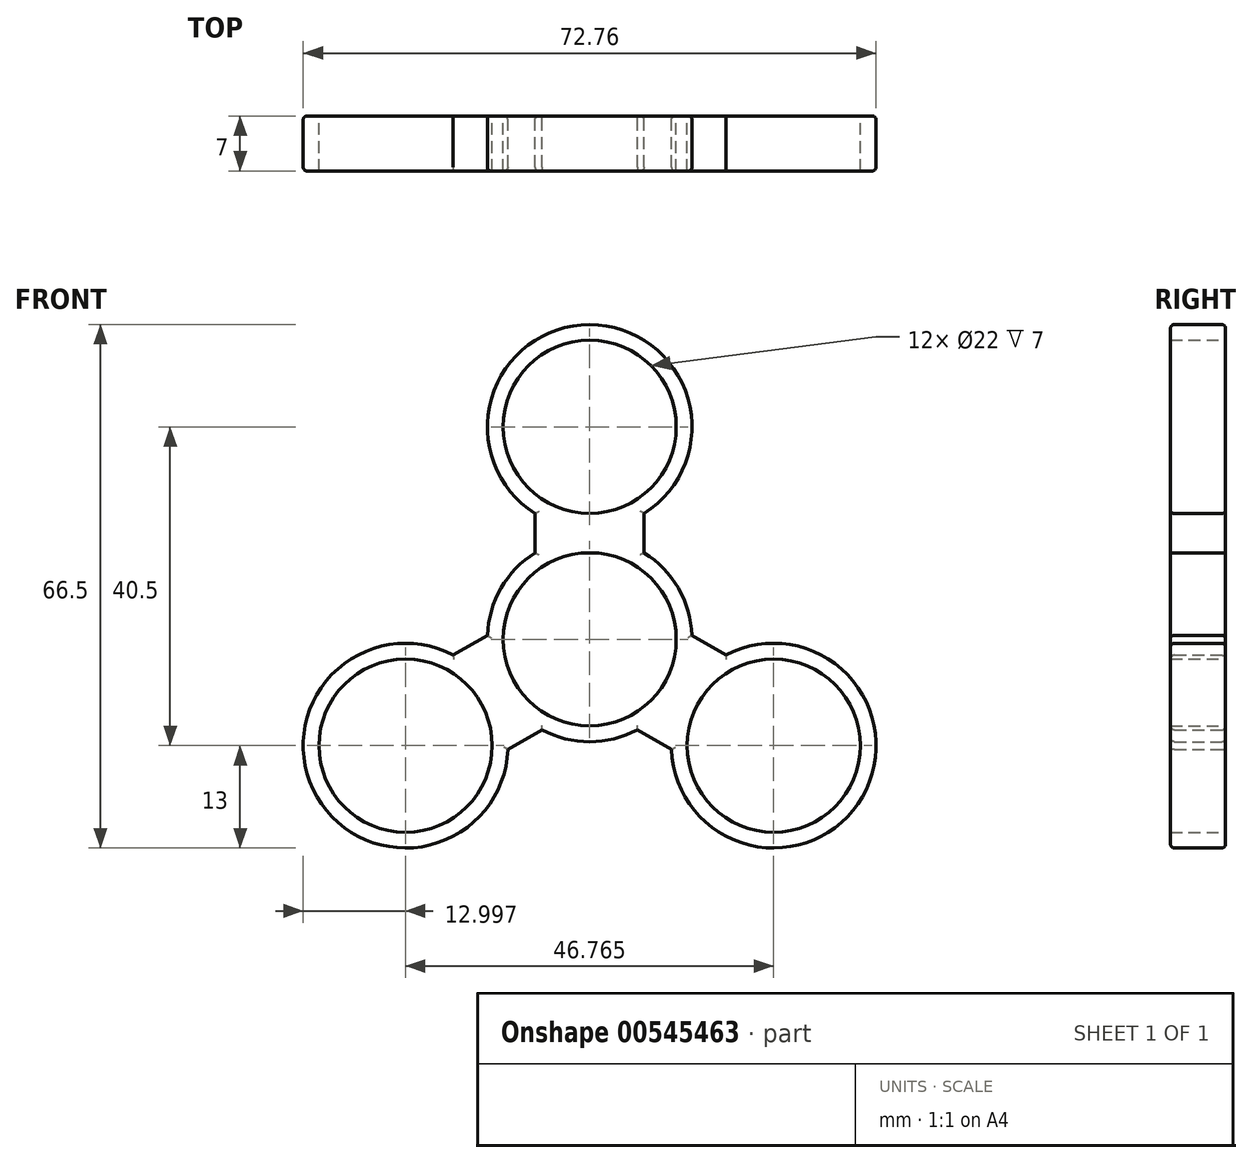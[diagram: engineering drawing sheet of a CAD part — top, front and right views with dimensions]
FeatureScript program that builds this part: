
annotation { "Feature Type Name" : "Feature", "Feature Type Description" : "" }
export const myFeature = defineFeature(function(context is Context, id is Id, definition is map)
    precondition{}
    {
        {
            var Q0;
            Q0=qCreatedBy(makeId("Front.planeOp"),FACE);
            var sketch = newSketch(context, id + "F0", { "sketchPlane" : qUnion([Q0])});
            skCircle(sketch, "E0", {"center": v(0, 0) * mm, "radius": 11 * mm});
            skCircle(sketch, "E1", {"center": v(0, 0) * mm, "radius": 13 * mm});
            skPoint(sketch, "E2", {"position": v(0, 27) * mm});
            skCircle(sketch, "E3", {"center": v(0, 27) * mm, "radius": 11 * mm});
            skCircle(sketch, "E4", {"center": v(0, 27) * mm, "radius": 13 * mm});
            skLineSegment(sketch, "E5", {"start": v(0, 0) * mm, "end": v(23.38, -13.5) * mm});
            skCircle(sketch, "E6", {"center": v(23.38, -13.5) * mm, "radius": 11 * mm});
            skCircle(sketch, "E7", {"center": v(23.38, -13.5) * mm, "radius": 13 * mm});
            skLineSegment(sketch, "E8", {"start": v(0, 0) * mm, "end": v(-23.38, -13.5) * mm});
            skCircle(sketch, "E9", {"center": v(-23.38, -13.5) * mm, "radius": 11 * mm});
            skCircle(sketch, "E10", {"center": v(-23.38, -13.5) * mm, "radius": 13 * mm});
            skLineSegment(sketch, "E11.left", {"start": v(6.93, 16) * mm, "end": v(6.93, 11) * mm});
            skLineSegment(sketch, "E11.right", {"start": v(-6.93, 16) * mm, "end": v(-6.93, 11) * mm});
            skPoint(sketch, "E11.middle", {"position": v(0, 13.5) * mm});
            skLineSegment(sketch, "E12", {"start": v(13, 0.5) * mm, "end": v(17.32, -2) * mm});
            skLineSegment(sketch, "E13", {"start": v(6.06, -11.5) * mm, "end": v(10.4, -14) * mm});
            skLineSegment(sketch, "E14", {"start": v(-17.32, -2) * mm, "end": v(-13, 0.5) * mm});
            skLineSegment(sketch, "E15", {"start": v(-10.4, -14) * mm, "end": v(-6.06, -11.5) * mm});
            skSolve(sketch);
        }
        {
            var Q0;
            Q0 = qSketchRegion(id + "F0", true);
            extrude(context, id + "F1", {"entities" : qUnion([Q0]), "endBound" : BoundingType.SYMMETRIC, "depth" : 7 * mm, "offsetDistance" : 25.4 * mm});
        }
        {
            var Q0;
            Q0=makeQuery(id+"F1.opExtrude","CAP_EDGE",EDGE,{"disambiguationData":[OSD([sQuery(id+"F0.wireOp",EDGE,"E4")])],"isStart":false});
            var Q1;
            Q1=makeQuery(id+"F1.opExtrude","CAP_EDGE",EDGE,{"disambiguationData":[OSD([sQuery(id+"F0.wireOp",EDGE,"E4")])],"isStart":true});
            var Q2;
            Q2=makeQuery(id+"F1.opExtrude","CAP_EDGE",EDGE,{"disambiguationData":[OSD([sQuery(id+"F0.wireOp",EDGE,"E11.left")])],"isStart":false});
            var Q3;
            Q3=makeQuery(id+"F1.opExtrude","CAP_EDGE",EDGE,{"disambiguationData":[OSD([sQuery(id+"F0.wireOp",EDGE,"E11.left")])],"isStart":true});
            var Q4;
            Q4=makeQuery(id+"F1.opExtrude","CAP_EDGE",EDGE,{"disambiguationData":[OSD([sQuery(id+"F0.wireOp",EDGE,"E11.right")])],"isStart":false});
            var Q5;
            Q5=makeQuery(id+"F1.opExtrude","CAP_EDGE",EDGE,{"disambiguationData":[OSD([sQuery(id+"F0.wireOp",EDGE,"E11.right")])],"isStart":true});
            var Q6;
            {var subQ0=sQuery(id+"F0.wireOp",EDGE,"E1");Q6=makeQuery(id+"F1.opExtrude","CAP_EDGE",EDGE,{"disambiguationData":[OSD([subQ0]),TDD([makeQuery(id+"F0.imprint","IMPRINT",EDGE,{"disambiguationData":[TD([[makeQuery(id+"F0.imprint","INTERSECT",VERTEX,{"derivedFrom":[subQ0,sQuery(id+"F0.wireOp",EDGE,"E11.right")]}),-1.0]])],"derivedFrom":subQ0})])],"isStart":true});}
            var Q7;
            {var subQ0=sQuery(id+"F0.wireOp",EDGE,"E1");Q7=makeQuery(id+"F1.opExtrude","CAP_EDGE",EDGE,{"disambiguationData":[OSD([subQ0]),TDD([makeQuery(id+"F0.imprint","IMPRINT",EDGE,{"disambiguationData":[TD([[makeQuery(id+"F0.imprint","INTERSECT",VERTEX,{"derivedFrom":[subQ0,sQuery(id+"F0.wireOp",EDGE,"E11.right")]}),-1.0]])],"derivedFrom":subQ0})])],"isStart":false});}
            var Q8;
            Q8=makeQuery(id+"F1.opExtrude","CAP_EDGE",EDGE,{"disambiguationData":[OSD([sQuery(id+"F0.wireOp",EDGE,"E14")])],"isStart":true});
            var Q9;
            Q9=makeQuery(id+"F1.opExtrude","CAP_EDGE",EDGE,{"disambiguationData":[OSD([sQuery(id+"F0.wireOp",EDGE,"E15")])],"isStart":true});
            var Q10;
            Q10=makeQuery(id+"F1.opExtrude","CAP_EDGE",EDGE,{"disambiguationData":[OSD([sQuery(id+"F0.wireOp",EDGE,"E10")])],"isStart":true});
            var Q11;
            Q11=makeQuery(id+"F1.opExtrude","CAP_EDGE",EDGE,{"disambiguationData":[OSD([sQuery(id+"F0.wireOp",EDGE,"E10")])],"isStart":false});
            var Q12;
            Q12=makeQuery(id+"F1.opExtrude","CAP_EDGE",EDGE,{"disambiguationData":[OSD([sQuery(id+"F0.wireOp",EDGE,"E14")])],"isStart":false});
            var Q13;
            Q13=makeQuery(id+"F1.opExtrude","CAP_EDGE",EDGE,{"disambiguationData":[OSD([sQuery(id+"F0.wireOp",EDGE,"E15")])],"isStart":false});
            var Q14;
            {var subQ0=sQuery(id+"F0.wireOp",EDGE,"E1");Q14=makeQuery(id+"F1.opExtrude","CAP_EDGE",EDGE,{"disambiguationData":[OSD([subQ0]),TDD([makeQuery(id+"F0.imprint","IMPRINT",EDGE,{"disambiguationData":[TD([[makeQuery(id+"F0.imprint","INTERSECT",VERTEX,{"derivedFrom":[subQ0,sQuery(id+"F0.wireOp",EDGE,"E13")]}),1.0]])],"derivedFrom":subQ0})])],"isStart":false});}
            var Q15;
            {var subQ0=sQuery(id+"F0.wireOp",EDGE,"E1");Q15=makeQuery(id+"F1.opExtrude","CAP_EDGE",EDGE,{"disambiguationData":[OSD([subQ0]),TDD([makeQuery(id+"F0.imprint","IMPRINT",EDGE,{"disambiguationData":[TD([[makeQuery(id+"F0.imprint","INTERSECT",VERTEX,{"derivedFrom":[subQ0,sQuery(id+"F0.wireOp",EDGE,"E13")]}),1.0]])],"derivedFrom":subQ0})])],"isStart":true});}
            var Q16;
            Q16=makeQuery(id+"F1.opExtrude","CAP_EDGE",EDGE,{"disambiguationData":[OSD([sQuery(id+"F0.wireOp",EDGE,"E13")])],"isStart":false});
            var Q17;
            Q17=makeQuery(id+"F1.opExtrude","CAP_EDGE",EDGE,{"disambiguationData":[OSD([sQuery(id+"F0.wireOp",EDGE,"E7")])],"isStart":false});
            var Q18;
            Q18=makeQuery(id+"F1.opExtrude","CAP_EDGE",EDGE,{"disambiguationData":[OSD([sQuery(id+"F0.wireOp",EDGE,"E7")])],"isStart":true});
            var Q19;
            Q19=makeQuery(id+"F1.opExtrude","CAP_EDGE",EDGE,{"disambiguationData":[OSD([sQuery(id+"F0.wireOp",EDGE,"E13")])],"isStart":true});
            var Q20;
            Q20=makeQuery(id+"F1.opExtrude","CAP_EDGE",EDGE,{"disambiguationData":[OSD([sQuery(id+"F0.wireOp",EDGE,"E12")])],"isStart":false});
            var Q21;
            Q21=makeQuery(id+"F1.opExtrude","CAP_EDGE",EDGE,{"disambiguationData":[OSD([sQuery(id+"F0.wireOp",EDGE,"E12")])],"isStart":true});
            var Q22;
            {var subQ0=sQuery(id+"F0.wireOp",EDGE,"E1");Q22=makeQuery(id+"F1.opExtrude","CAP_EDGE",EDGE,{"disambiguationData":[OSD([subQ0]),TDD([makeQuery(id+"F0.imprint","IMPRINT",EDGE,{"disambiguationData":[TD([[makeQuery(id+"F0.imprint","INTERSECT",VERTEX,{"derivedFrom":[subQ0,sQuery(id+"F0.wireOp",EDGE,"E11.left")]}),1.0]])],"derivedFrom":subQ0})])],"isStart":true});}
            var Q23;
            {var subQ0=sQuery(id+"F0.wireOp",EDGE,"E1");Q23=makeQuery(id+"F1.opExtrude","CAP_EDGE",EDGE,{"disambiguationData":[OSD([subQ0]),TDD([makeQuery(id+"F0.imprint","IMPRINT",EDGE,{"disambiguationData":[TD([[makeQuery(id+"F0.imprint","INTERSECT",VERTEX,{"derivedFrom":[subQ0,sQuery(id+"F0.wireOp",EDGE,"E11.left")]}),1.0]])],"derivedFrom":subQ0})])],"isStart":false});}
            fillet(context, id + "F2", {"entities" : qUnion([Q0, Q1, Q2, Q3, Q4, Q5, Q6, Q7, Q8, Q9, Q10, Q11, Q12, Q13, Q14, Q15, Q16, Q17, Q18, Q19, Q20, Q21, Q22, Q23]), "radius" : 0.5 * mm, "tangentPropagation" : true, "allowEdgeOverflow" : false});
        }
    });
